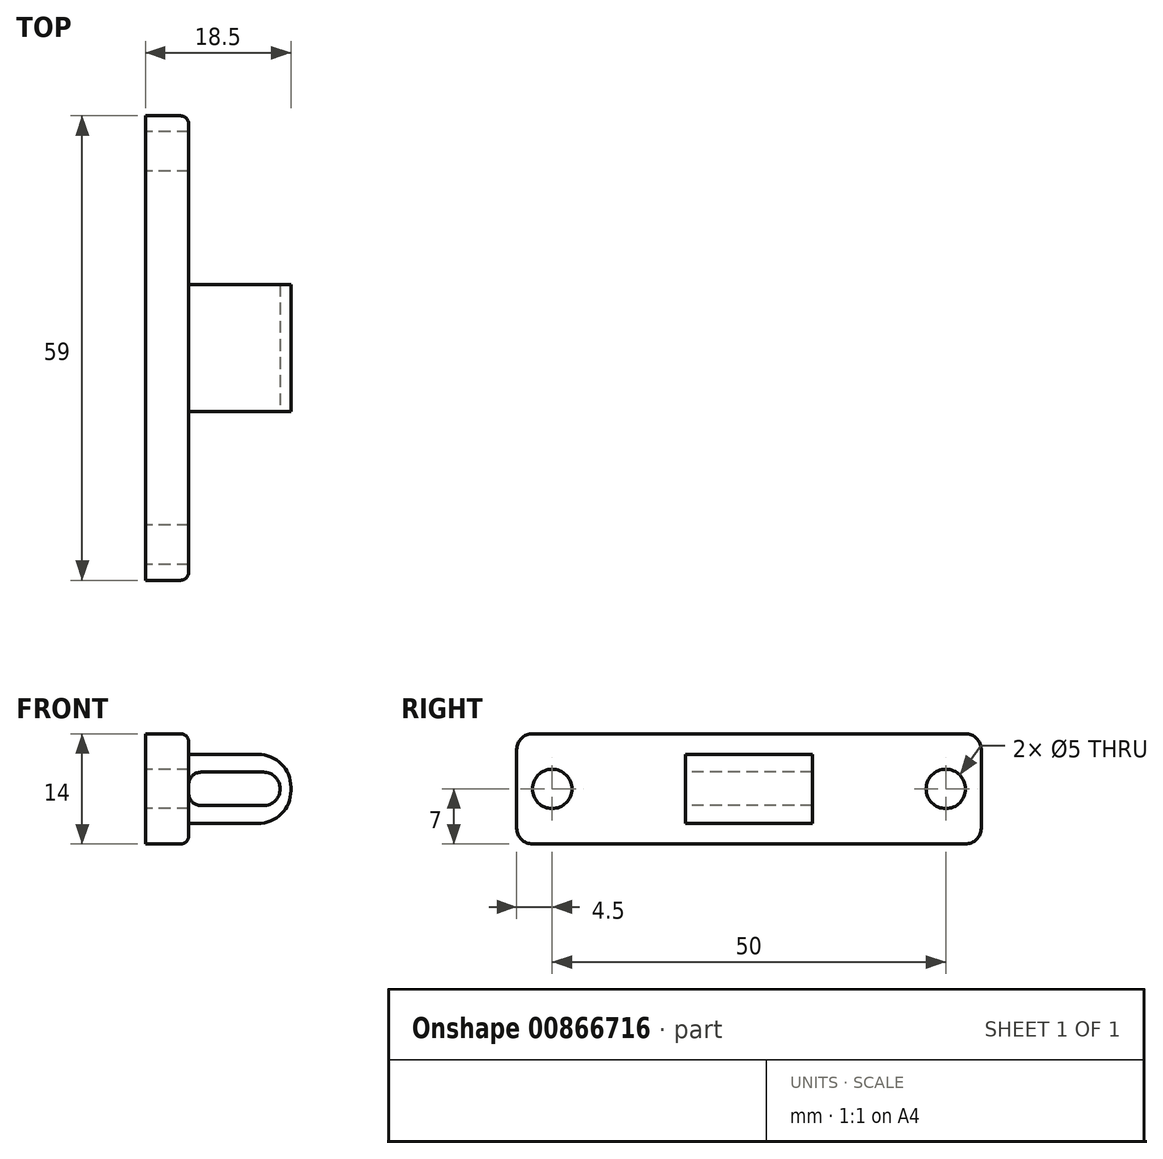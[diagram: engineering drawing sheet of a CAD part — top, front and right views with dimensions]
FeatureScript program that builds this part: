
annotation { "Feature Type Name" : "Feature", "Feature Type Description" : "" }
export const myFeature = defineFeature(function(context is Context, id is Id, definition is map)
    precondition{}
    {
        {
            var Q0;
            Q0=qCreatedBy(makeId("Right.planeOp"),FACE);
            var sketch = newSketch(context, id + "F0", { "sketchPlane" : qUnion([Q0])});
            skLineSegment(sketch, "E0.bottom", {"start": v(-29.5, -7) * mm, "end": v(29.5, -7) * mm});
            skLineSegment(sketch, "E0.top", {"start": v(-29.5, 7) * mm, "end": v(29.5, 7) * mm});
            skLineSegment(sketch, "E0.left", {"start": v(-29.5, -7) * mm, "end": v(-29.5, 7) * mm});
            skLineSegment(sketch, "E0.right", {"start": v(29.5, -7) * mm, "end": v(29.5, 7) * mm});
            skPoint(sketch, "E0.middle", {"position": v(0, 0) * mm});
            skCircle(sketch, "E1", {"center": v(0, 0) * mm, "radius": 2.5 * mm});
            skCircle(sketch, "E2", {"center": v(-25, 0) * mm, "radius": 2.5 * mm});
            skCircle(sketch, "E3", {"center": v(25, 0) * mm, "radius": 2.5 * mm});
            skLineSegment(sketch, "E4.bottom", {"start": v(-8.05, -4.4) * mm, "end": v(8.05, -4.4) * mm});
            skLineSegment(sketch, "E4.top", {"start": v(-8.05, 4.4) * mm, "end": v(8.05, 4.4) * mm});
            skLineSegment(sketch, "E4.left", {"start": v(-8.05, -4.4) * mm, "end": v(-8.05, 4.4) * mm});
            skLineSegment(sketch, "E4.right", {"start": v(8.05, -4.4) * mm, "end": v(8.05, 4.4) * mm});
            skSolve(sketch);
        }
        {
            var Q0;
            Q0 = qSketchRegion(id + "F0", true);
            extrude(context, id + "F1", {"entities" : qUnion([Q0]), "depth" : 5.5 * mm, "offsetDistance" : 25 * mm});
        }
        {
            var Q0;
            Q0=makeQuery(id+"F0.imprint","IMPRINT",FACE,{"disambiguationData":[TD([[makeQuery(id+"F0.imprint","IMPRINT",EDGE,{"derivedFrom":sQuery(id+"F0.wireOp",EDGE,"E1")}),-1.0]])]});
            var Q1;
            Q1=makeQuery(id+"F0.imprint","IMPRINT",FACE,{"disambiguationData":[TD([[makeQuery(id+"F0.imprint","IMPRINT",EDGE,{"derivedFrom":sQuery(id+"F0.wireOp",EDGE,"E1")}),1.0]])]});
            extrude(context, id + "F2", {"entities" : qUnion([Q0, Q1]), "operationType" : NewBodyOperationType.ADD, "depth" : 18.5 * mm, "offsetDistance" : 25 * mm});
        }
        {
            var Q0;
            Q0=makeQuery(id+"F2.opExtrude","CAP_EDGE",EDGE,{"disambiguationData":[OSD([sQuery(id+"F0.wireOp",EDGE,"E4.top")])],"isStart":false});
            var Q1;
            Q1=makeQuery(id+"F2.opExtrude","CAP_EDGE",EDGE,{"disambiguationData":[OSD([sQuery(id+"F0.wireOp",EDGE,"E4.bottom")])],"isStart":false});
            fillet(context, id + "F3", {"entities" : qUnion([Q0, Q1]), "radius" : 4.2 * mm, "tangentPropagation" : true, "allowEdgeOverflow" : false});
        }
        {
            var Q0;
            Q0=makeQuery(id+"F1.opExtrude","SWEPT_EDGE",EDGE,{"disambiguationData":[OSD([sQuery(id+"F0.wireOp",EDGE,"E0.top"),sQuery(id+"F0.wireOp",EDGE,"E0.right")])]});
            var Q1;
            Q1=makeQuery(id+"F1.opExtrude","SWEPT_EDGE",EDGE,{"disambiguationData":[OSD([sQuery(id+"F0.wireOp",EDGE,"E0.bottom"),sQuery(id+"F0.wireOp",EDGE,"E0.right")])]});
            var Q2;
            Q2=makeQuery(id+"F1.opExtrude","SWEPT_EDGE",EDGE,{"disambiguationData":[OSD([sQuery(id+"F0.wireOp",EDGE,"E0.top"),sQuery(id+"F0.wireOp",EDGE,"E0.left")])]});
            var Q3;
            Q3=makeQuery(id+"F1.opExtrude","SWEPT_EDGE",EDGE,{"disambiguationData":[OSD([sQuery(id+"F0.wireOp",EDGE,"E0.bottom"),sQuery(id+"F0.wireOp",EDGE,"E0.left")])]});
            fillet(context, id + "F4", {"entities" : qUnion([Q0, Q1, Q2, Q3]), "radius" : 2 * mm, "tangentPropagation" : true, "allowEdgeOverflow" : false});
        }
        {
            var Q0;
            Q0=makeQuery(id+"F1.opExtrude","CAP_EDGE",EDGE,{"disambiguationData":[OSD([sQuery(id+"F0.wireOp",EDGE,"E0.top")])],"isStart":false});
            fillet(context, id + "F5", {"entities" : qUnion([Q0]), "radius" : 1 * mm, "tangentPropagation" : true, "allowEdgeOverflow" : false});
        }
        {
            var Q0;
            Q0=makeQuery(id+"F2.opExtrude","SWEPT_FACE",FACE,{"disambiguationData":[OSD([sQuery(id+"F0.wireOp",EDGE,"E4.left")])]});
            var sketch = newSketch(context, id + "F6", { "sketchPlane" : qUnion([Q0])});
            skLineSegment(sketch, "E5.bottom", {"start": v(5.5, -2.12) * mm, "end": v(15, -2.12) * mm});
            skLineSegment(sketch, "E5.top", {"start": v(5.5, 2.13) * mm, "end": v(15, 2.13) * mm});
            skLineSegment(sketch, "E5.left", {"start": v(5.5, -2.12) * mm, "end": v(5.5, 2.13) * mm});
            skPoint(sketch, "E5.middle", {"position": v(10.25, 0) * mm});
            skArc(sketch, "E6", {"start": v(15, -2.12) * mm, "mid": v(17.12, 0) * mm, "end": v(15, 2.13) * mm});
            skSolve(sketch);
        }
        {
            var Q0;
            Q0=makeQuery(id+"F6.imprint","IMPRINT",FACE,{"disambiguationData":[TD([[makeQuery(id+"F6.imprint","IMPRINT",EDGE,{"derivedFrom":sQuery(id+"F6.wireOp",EDGE,"E5.bottom")}),1.0]])]});
            extrude(context, id + "F7", {"entities" : qUnion([Q0]), "operationType" : NewBodyOperationType.REMOVE, "oppositeDirection" : true, "depth" : 25 * mm, "offsetDistance" : 25 * mm});
        }
        {
            var Q0;
            Q0=makeQuery(id+"F1.opExtrude","CAP_EDGE",EDGE,{"disambiguationData":[OSD([sQuery(id+"F0.wireOp",EDGE,"E4.top")])],"isStart":false});
            var Q1;
            Q1=makeQuery(id+"F1.opExtrude","CAP_EDGE",EDGE,{"disambiguationData":[OSD([sQuery(id+"F0.wireOp",EDGE,"E4.bottom")])],"isStart":false});
            var Q2;
            Q2=makeQuery(id+"F7.boolean.opBoolean","COPY",EDGE,{"derivedFrom":makeQuery(id+"F7.opExtrude","SWEPT_EDGE",EDGE,{"disambiguationData":[OSD([sQuery(id+"F0.wireOp",EDGE,"E4.left"),sQuery(id+"F6.wireOp",EDGE,"E5.bottom"),sQuery(id+"F6.wireOp",EDGE,"E5.left")])]})});
            var Q3;
            Q3=makeQuery(id+"F7.boolean.opBoolean","COPY",EDGE,{"derivedFrom":makeQuery(id+"F7.opExtrude","SWEPT_EDGE",EDGE,{"disambiguationData":[OSD([sQuery(id+"F0.wireOp",EDGE,"E4.left"),sQuery(id+"F6.wireOp",EDGE,"E5.top"),sQuery(id+"F6.wireOp",EDGE,"E5.left")])]})});
            fillet(context, id + "F8", {"entities" : qUnion([Q0, Q1, Q2, Q3]), "radius" : 1.6 * mm, "tangentPropagation" : true, "allowEdgeOverflow" : false});
        }
    });
